# Revit family: LEPC22-24
name_source: partatom
category: Lighting Fixtures
units: mm (PartAtom-declared; Revit-internal decimal feet)

## family parameters
Cut with Voids When Loaded = No
Host = Face
Light Source = Yes
OmniClass Number = 23.80.70.11
OmniClass Title = Luminaries for Internal Lighting
Part Type = Normal
Room Calculation Point = No
Round Connector Dimension = Use Diameter
Shared = Yes

## types (2) — shared parameters
Apparent Load = 0 VA
Backbox = White
Color Filter = 16777215
Default Elevation = 48"
Description = A e•poc® LED full distribution luminaire, with advanced solid state electronics, has significantly improved performance to offer additional lumen packages for maximum versatility.
Dimming Lamp Color Temperature Shift = <None>
Emit from Line Length = 12"
Glass = White Glass
Lumen Output = Very High Lumen
Manufacturer = Columbia Lighting
Model = LEPC24
Shielding = Low Lamp Image
Tilt Angle = -90.00°
URL = https://www.currentlighting.com
Voltage = 120 V

## per-type parameters (varying)
| type | Lamp | Length | Lighting Length | Nominal Watts | Photometric Web File |
| LEPC22-40VL-LL | LED Lamp | 24" | LEPC Light : LEPC2-2 | 41 W | LEPC22-40VL-LL.ies |
| LEPC24-40VL-LL | LED LAMP | 48" | LEPC Light : LEPC2-4 | 60 W | LEPC24-40VLG-LL-EDU.ies |

## geometry (parser evidence)
native form markers: Sweep x3
no freeform markers — native parametric forms only
